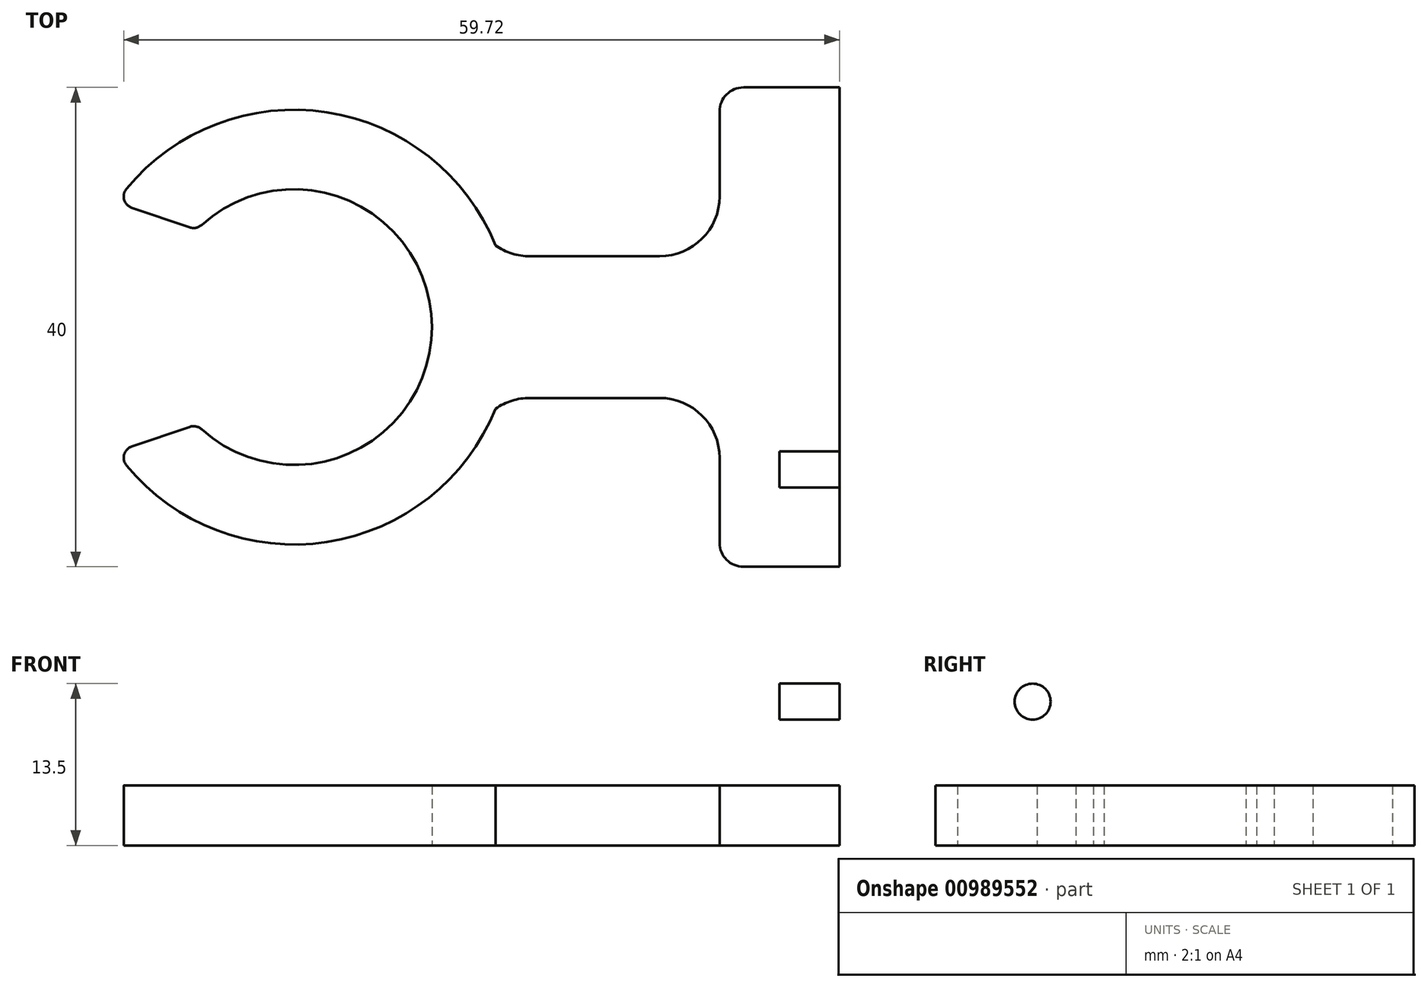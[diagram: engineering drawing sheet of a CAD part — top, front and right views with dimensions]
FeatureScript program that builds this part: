
annotation { "Feature Type Name" : "Feature", "Feature Type Description" : "" }
export const myFeature = defineFeature(function(context is Context, id is Id, definition is map)
    precondition{}
    {
        {
            var Q0;
            Q0=qCreatedBy(makeId("Top.planeOp"),FACE);
            var sketch = newSketch(context, id + "F0", { "sketchPlane" : qUnion([Q0])});
            skArc(sketch, "E0", {"start": v(-7.71, -8.53) * mm, "mid": v(11.5, 0) * mm, "end": v(-7.71, 8.53) * mm});
            skLineSegment(sketch, "E1", {"start": v(11.5, 0) * mm, "end": v(45.5, 0) * mm, "construction": true});
            skLineSegment(sketch, "E2", {"start": v(19.68, 5.91) * mm, "end": v(30.5, 5.91) * mm});
            skLineSegment(sketch, "E3", {"start": v(35.5, 10.91) * mm, "end": v(35.5, 18) * mm});
            skLineSegment(sketch, "E4", {"start": v(37.5, 20) * mm, "end": v(45.5, 20) * mm});
            skLineSegment(sketch, "E5", {"start": v(45.5, 20) * mm, "end": v(45.5, 0) * mm});
            skLineSegment(sketch, "E6.MirrorCS", {"start": v(19.68, -5.91) * mm, "end": v(30.5, -5.91) * mm});
            skLineSegment(sketch, "E7.MirrorCS", {"start": v(35.5, -10.91) * mm, "end": v(35.5, -18) * mm});
            skLineSegment(sketch, "E8.MirrorCS", {"start": v(37.5, -20) * mm, "end": v(45.5, -20) * mm});
            skLineSegment(sketch, "E9.MirrorCS", {"start": v(45.5, -20) * mm, "end": v(45.5, 0) * mm});
            skPoint(sketch, "E10.newPointB", {"position": v(16.43, 5.91) * mm});
            skArc(sketch, "E10.filletArc", {"start": v(16.81, 6.81) * mm, "mid": v(18.17, 6.14) * mm, "end": v(19.68, 5.91) * mm});
            skPoint(sketch, "E11.visualSharp", {"position": v(35.5, 5.91) * mm});
            skArc(sketch, "E11.filletArc", {"start": v(30.5, 5.91) * mm, "mid": v(34.04, 7.37) * mm, "end": v(35.5, 10.91) * mm});
            skArc(sketch, "E12.MirrorCS", {"start": v(16.81, -6.81) * mm, "mid": v(18.17, -6.14) * mm, "end": v(19.68, -5.91) * mm});
            skArc(sketch, "E13.MirrorCS", {"start": v(30.5, -5.91) * mm, "mid": v(34.04, -7.37) * mm, "end": v(35.5, -10.91) * mm});
            skPoint(sketch, "E14.orphan", {"position": v(35.5, -5.91) * mm});
            skPoint(sketch, "E15.orphan", {"position": v(16.43, -5.91) * mm});
            skPoint(sketch, "E16.visualSharp", {"position": v(35.5, 20) * mm});
            skArc(sketch, "E16.filletArc", {"start": v(37.5, 20) * mm, "mid": v(36.09, 19.41) * mm, "end": v(35.5, 18) * mm});
            skPoint(sketch, "E17.visualSharp", {"position": v(35.5, -20) * mm});
            skArc(sketch, "E17.filletArc", {"start": v(35.5, -18) * mm, "mid": v(36.09, -19.41) * mm, "end": v(37.5, -20) * mm});
            skArc(sketch, "E18", {"start": v(-14.26, -11.2) * mm, "mid": v(2.54, -17.96) * mm, "end": v(16.81, -6.81) * mm});
            skArc(sketch, "E19.MirrorCS", {"start": v(-14, 11.54) * mm, "mid": v(2.75, 17.93) * mm, "end": v(16.81, 6.81) * mm});
            skPoint(sketch, "E20.orphan", {"position": v(15.3, 8.49) * mm});
            skPoint(sketch, "E21.MirrorCS.start.orphan", {"position": v(15.3, -8.49) * mm});
            skPoint(sketch, "E22.trimOffspring.end.orphan", {"position": v(-5.3, -4.93) * mm});
            skArc(sketch, "E23.trimOffspring", {"start": v(16.81, 6.81) * mm, "mid": v(2.75, 17.93) * mm, "end": v(-14, 11.54) * mm});
            skArc(sketch, "E24.trimOffspring", {"start": v(16.81, -6.81) * mm, "mid": v(2.75, -17.93) * mm, "end": v(-14, -11.54) * mm});
            skLineSegment(sketch, "E25", {"start": v(0, 0) * mm, "end": v(-17.76, -17.76) * mm, "construction": true});
            skPoint(sketch, "E26.trimOffspring.end.orphan", {"position": v(-5.3, 4.93) * mm});
            skLineSegment(sketch, "E27", {"start": v(0, 0) * mm, "end": v(-17.28, -12.1) * mm, "construction": true});
            skLineSegment(sketch, "E28", {"start": v(-8.7, -8.32) * mm, "end": v(-13.54, -9.96) * mm});
            skPoint(sketch, "E29.visualSharp", {"position": v(-8.13, -8.13) * mm});
            skArc(sketch, "E29.filletArc", {"start": v(-7.71, -8.53) * mm, "mid": v(-8.18, -8.3) * mm, "end": v(-8.7, -8.32) * mm});
            skArc(sketch, "E30.filletArc", {"start": v(-13.54, -9.96) * mm, "mid": v(-14.18, -10.63) * mm, "end": v(-14, -11.54) * mm});
            skLineSegment(sketch, "E31.MirrorCS", {"start": v(-8.7, 8.32) * mm, "end": v(-13.54, 9.96) * mm});
            skArc(sketch, "E32.MirrorCS", {"start": v(-13.54, 9.96) * mm, "mid": v(-14.18, 10.63) * mm, "end": v(-14, 11.54) * mm});
            skArc(sketch, "E33.MirrorCS", {"start": v(-7.71, 8.53) * mm, "mid": v(-8.18, 8.3) * mm, "end": v(-8.7, 8.32) * mm});
            skSolve(sketch);
        }
        {
            var Q0;
            Q0=makeQuery(id+"F0.imprint","IMPRINT",FACE,{"disambiguationData":[TD([[makeQuery(id+"F0.imprint","IMPRINT",EDGE,{"derivedFrom":sQuery(id+"F0.wireOp",EDGE,"E0")}),-1.0]])]});
            extrude(context, id + "F1", {"entities" : qUnion([Q0]), "depth" : 5 * mm, "offsetDistance" : 25 * mm});
        }
        {
            var Q0;
            Q0=makeQuery(id+"F1.opExtrude","CAP_FACE",FACE,{"disambiguationData":[OSD([sQuery(id+"F0.wireOp",EDGE,"E0"),sQuery(id+"F0.wireOp",EDGE,"E2"),sQuery(id+"F0.wireOp",EDGE,"E3"),sQuery(id+"F0.wireOp",EDGE,"E4"),sQuery(id+"F0.wireOp",EDGE,"E5"),sQuery(id+"F0.wireOp",EDGE,"E6.MirrorCS"),sQuery(id+"F0.wireOp",EDGE,"E7.MirrorCS"),sQuery(id+"F0.wireOp",EDGE,"E8.MirrorCS"),sQuery(id+"F0.wireOp",EDGE,"E9.MirrorCS"),sQuery(id+"F0.wireOp",EDGE,"E10.filletArc"),sQuery(id+"F0.wireOp",EDGE,"E11.filletArc"),sQuery(id+"F0.wireOp",EDGE,"E12.MirrorCS"),sQuery(id+"F0.wireOp",EDGE,"E13.MirrorCS"),sQuery(id+"F0.wireOp",EDGE,"E16.filletArc"),sQuery(id+"F0.wireOp",EDGE,"E17.filletArc"),sQuery(id+"F0.wireOp",EDGE,"E18"),sQuery(id+"F0.wireOp",EDGE,"E19.MirrorCS"),sQuery(id+"F0.wireOp",EDGE,"E28"),sQuery(id+"F0.wireOp",EDGE,"E29.filletArc"),sQuery(id+"F0.wireOp",EDGE,"E30.filletArc"),sQuery(id+"F0.wireOp",EDGE,"E31.MirrorCS"),sQuery(id+"F0.wireOp",EDGE,"E32.MirrorCS"),sQuery(id+"F0.wireOp",EDGE,"E33.MirrorCS")])],"isStart":false});
            var sketch = newSketch(context, id + "F2", { "sketchPlane" : qUnion([Q0])});
            skLineSegment(sketch, "E34.bottom", {"start": v(45.5, 20) * mm, "end": v(40.5, 20) * mm});
            skLineSegment(sketch, "E34.top", {"start": v(45.5, -20) * mm, "end": v(40.5, -20) * mm});
            skLineSegment(sketch, "E34.left", {"start": v(45.5, 20) * mm, "end": v(45.5, -20) * mm});
            skLineSegment(sketch, "E34.right", {"start": v(40.5, 20) * mm, "end": v(40.5, -20) * mm});
            skSolve(sketch);
        }
        {
            var Q0;
            Q0=makeQuery(id+"F2.imprint","IMPRINT",FACE,{"disambiguationData":[TD([[makeQuery(id+"F2.imprint","IMPRINT",EDGE,{"derivedFrom":sQuery(id+"F2.wireOp",EDGE,"E34.bottom")}),-1.0]])]});
            extrude(context, id + "F3", {"entities" : qUnion([Q0]), "operationType" : NewBodyOperationType.ADD, "depth" : 12 * mm, "offsetDistance" : 25 * mm});
        }
        {
            var Q0;
            Q0=makeQuery(id+"F3.opExtrude","CAP_EDGE",EDGE,{"disambiguationData":[OSD([sQuery(id+"F2.wireOp",EDGE,"E34.right")])],"isStart":true});
            var Q1;
            Q1=makeQuery(id+"F3.opExtrude","CAP_EDGE",EDGE,{"disambiguationData":[OSD([sQuery(id+"F2.wireOp",EDGE,"E34.bottom")])],"isStart":false});
            var Q2;
            Q2=makeQuery(id+"F3.opExtrude","CAP_EDGE",EDGE,{"disambiguationData":[OSD([sQuery(id+"F2.wireOp",EDGE,"E34.top")])],"isStart":false});
            fillet(context, id + "F4", {"entities" : qUnion([Q0, Q1, Q2]), "radius" : 3 * mm, "tangentPropagation" : true, "allowEdgeOverflow" : false});
        }
        {
            var Q0;
            Q0=makeQuery(id+"F3.opExtrude","SWEPT_FACE",FACE,{"disambiguationData":[OSD([sQuery(id+"F2.wireOp",EDGE,"E34.right")])]});
            var sketch = newSketch(context, id + "F5", { "sketchPlane" : qUnion([Q0])});
            skLineSegment(sketch, "E35", {"start": v(-20, 12) * mm, "end": v(20, 12) * mm, "construction": true});
            skLineSegment(sketch, "E36", {"start": v(0, 17) * mm, "end": v(0, 12) * mm, "construction": true});
            skCircle(sketch, "E37", {"center": v(-11.88, 12) * mm, "radius": 1.5 * mm});
            skCircle(sketch, "E38.MirrorC", {"center": v(11.88, 12) * mm, "radius": 1.5 * mm});
            skSolve(sketch);
        }
        {
            var Q0;
            Q0=makeQuery(id+"F5.imprint","IMPRINT",FACE,{"disambiguationData":[TD([[makeQuery(id+"F5.imprint","IMPRINT",EDGE,{"derivedFrom":sQuery(id+"F5.wireOp",EDGE,"E37")}),1.0]])]});
            var Q1;
            Q1=makeQuery(id+"F5.imprint","IMPRINT",FACE,{"disambiguationData":[TD([[makeQuery(id+"F5.imprint","IMPRINT",EDGE,{"derivedFrom":sQuery(id+"F5.wireOp",EDGE,"E38.MirrorC")}),-1.0]])]});
            extrude(context, id + "F6", {"entities" : qUnion([Q0, Q1]), "operationType" : NewBodyOperationType.REMOVE, "oppositeDirection" : true, "depth" : 10 * mm, "offsetDistance" : 25 * mm});
        }
    });
